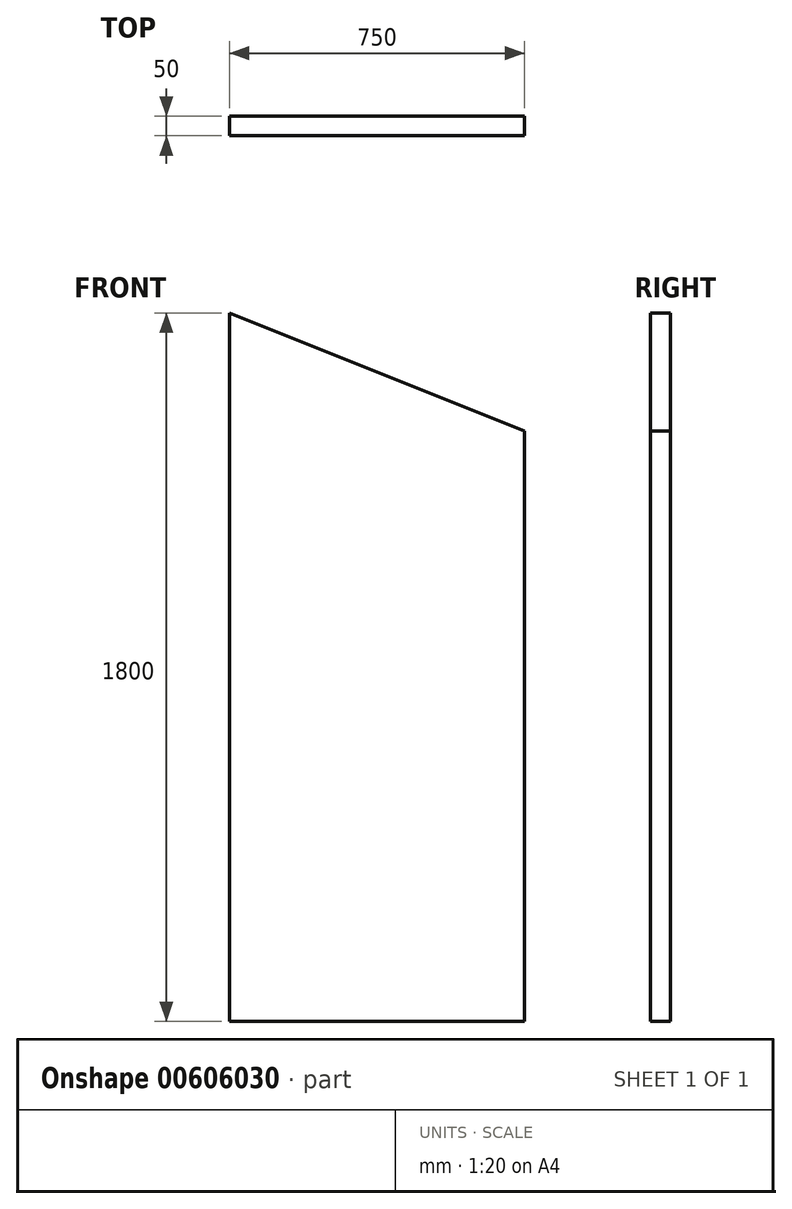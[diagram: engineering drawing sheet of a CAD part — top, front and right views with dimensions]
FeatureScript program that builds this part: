
annotation { "Feature Type Name" : "Feature", "Feature Type Description" : "" }
export const myFeature = defineFeature(function(context is Context, id is Id, definition is map)
    precondition{}
    {
        {
            var Q0;
            Q0=qCreatedBy(makeId("Front.planeOp"),FACE);
            var sketch = newSketch(context, id + "F0", { "sketchPlane" : qUnion([Q0])});
            skLineSegment(sketch, "E0.top", {"start": v(375, -900) * mm, "end": v(-375, -900) * mm});
            skLineSegment(sketch, "E0.right", {"start": v(-375, 900) * mm, "end": v(-375, -900) * mm});
            skPoint(sketch, "E0.middle", {"position": v(0, 0) * mm});
            skLineSegment(sketch, "E1", {"start": v(375, 600) * mm, "end": v(-375, 900) * mm});
            skLineSegment(sketch, "E2", {"start": v(375, 600) * mm, "end": v(375, -900) * mm});
            skSolve(sketch);
        }
        {
            var Q0;
            Q0 = qSketchRegion(id + "F0", true);
            extrude(context, id + "F1", {"entities" : qUnion([Q0]), "depth" : 50 * mm, "offsetDistance" : 25.4 * mm});
        }
    });
